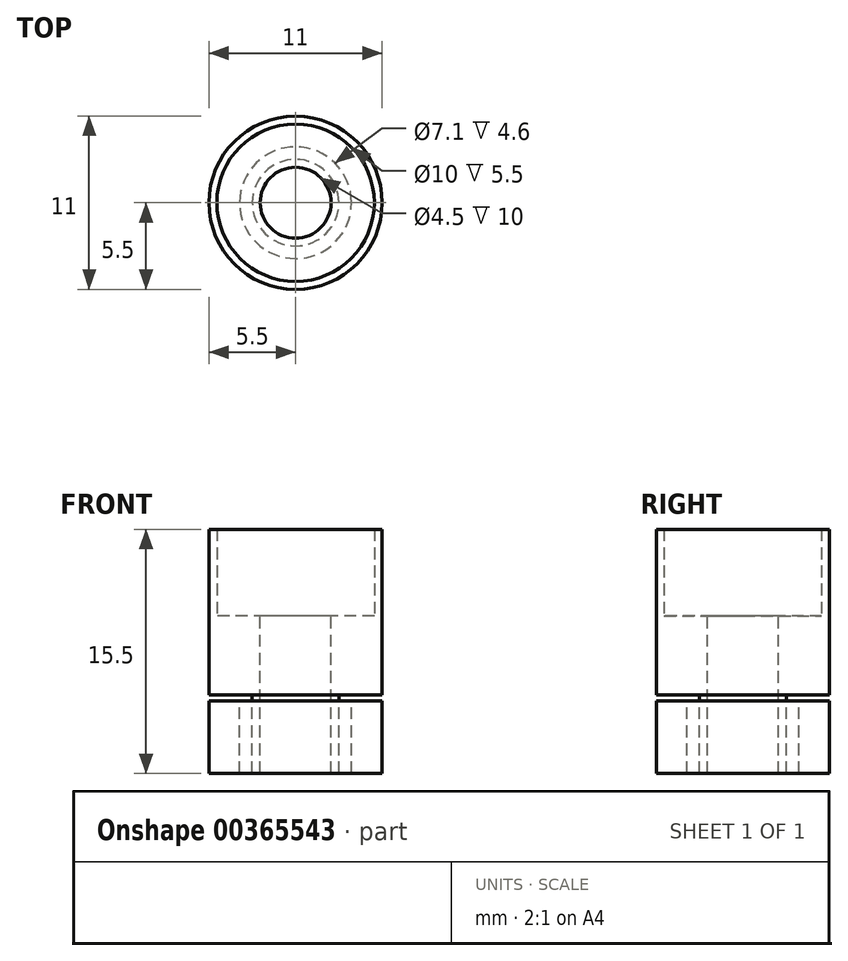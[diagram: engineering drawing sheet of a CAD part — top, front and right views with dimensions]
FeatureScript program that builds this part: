
annotation { "Feature Type Name" : "Feature", "Feature Type Description" : "" }
export const myFeature = defineFeature(function(context is Context, id is Id, definition is map)
    precondition{}
    {
        {
            var Q0;
            Q0=qCreatedBy(makeId("Top.planeOp"),FACE);
            var sketch = newSketch(context, id + "F0", { "sketchPlane" : qUnion([Q0])});
            skCircle(sketch, "E0", {"center": v(0, 0) * mm, "radius": 2.25 * mm});
            skCircle(sketch, "E1", {"center": v(0, 0) * mm, "radius": 5 * mm});
            skCircle(sketch, "E2", {"center": v(0, 0) * mm, "radius": 2.75 * mm});
            skCircle(sketch, "E3", {"center": v(0, 0) * mm, "radius": 5.5 * mm});
            skCircle(sketch, "E4.0", {"center": v(0, 0) * mm, "radius": 3.55 * mm});
            skSolve(sketch);
        }
        {
            var Q0;
            Q0=makeQuery(id+"F0.imprint","IMPRINT",FACE,{"disambiguationData":[TD([[makeQuery(id+"F0.imprint","IMPRINT",EDGE,{"derivedFrom":sQuery(id+"F0.wireOp",EDGE,"E1")}),-1.0]])]});
            extrude(context, id + "F1", {"entities" : qUnion([Q0]), "depth" : 5.5 * mm});
        }
        {
            var Q0;
            Q0=makeQuery(id+"F0.imprint","IMPRINT",FACE,{"disambiguationData":[TD([[makeQuery(id+"F0.imprint","IMPRINT",EDGE,{"derivedFrom":sQuery(id+"F0.wireOp",EDGE,"E1")}),1.0]])]});
            var Q1;
            Q1=makeQuery(id+"F0.imprint","IMPRINT",FACE,{"disambiguationData":[TD([[makeQuery(id+"F0.imprint","IMPRINT",EDGE,{"derivedFrom":sQuery(id+"F0.wireOp",EDGE,"E0")}),-1.0]])]});
            var Q2;
            Q2=makeQuery(id+"F0.imprint","IMPRINT",FACE,{"disambiguationData":[TD([[makeQuery(id+"F0.imprint","IMPRINT",EDGE,{"derivedFrom":sQuery(id+"F0.wireOp",EDGE,"E2")}),-1.0]])]});
            extrude(context, id + "F2", {"entities" : qUnion([Q0, Q1, Q2]), "oppositeDirection" : true, "depth" : 5 * mm});
        }
        {
            var Q0;
            Q0=makeQuery(id+"F0.imprint","IMPRINT",FACE,{"disambiguationData":[TD([[makeQuery(id+"F0.imprint","IMPRINT",EDGE,{"derivedFrom":sQuery(id+"F0.wireOp",EDGE,"E0")}),-1.0]])]});
            extrude(context, id + "F3", {"entities" : qUnion([Q0]), "operationType" : NewBodyOperationType.ADD, "oppositeDirection" : true, "depth" : (5 + 5) * mm});
        }
        {
            var Q0;
            Q0=makeQuery(id+"F0.imprint","IMPRINT",FACE,{"disambiguationData":[TD([[makeQuery(id+"F0.imprint","IMPRINT",EDGE,{"derivedFrom":sQuery(id+"F0.wireOp",EDGE,"E1")}),-1.0]])]});
            extrude(context, id + "F4", {"entities" : qUnion([Q0]), "operationType" : NewBodyOperationType.ADD, "oppositeDirection" : true, "depth" : 5 * mm});
        }
        {
            var Q0;
            Q0=makeQuery(id+"F0.imprint","IMPRINT",FACE,{"disambiguationData":[TD([[makeQuery(id+"F0.imprint","IMPRINT",EDGE,{"derivedFrom":sQuery(id+"F0.wireOp",EDGE,"E1")}),-1.0]])]});
            var Q1;
            Q1=makeQuery(id+"F0.imprint","IMPRINT",FACE,{"disambiguationData":[TD([[makeQuery(id+"F0.imprint","IMPRINT",EDGE,{"derivedFrom":sQuery(id+"F0.wireOp",EDGE,"E1")}),1.0]])]});
            extrude(context, id + "F5", {"entities" : qUnion([Q0, Q1]), "oppositeDirection" : true, "depth" : 10 * mm, "hasSecondDirection" : true, "secondDirectionOppositeDirection" : true, "secondDirectionDepth" : 5.4 * mm});
        }
    });
